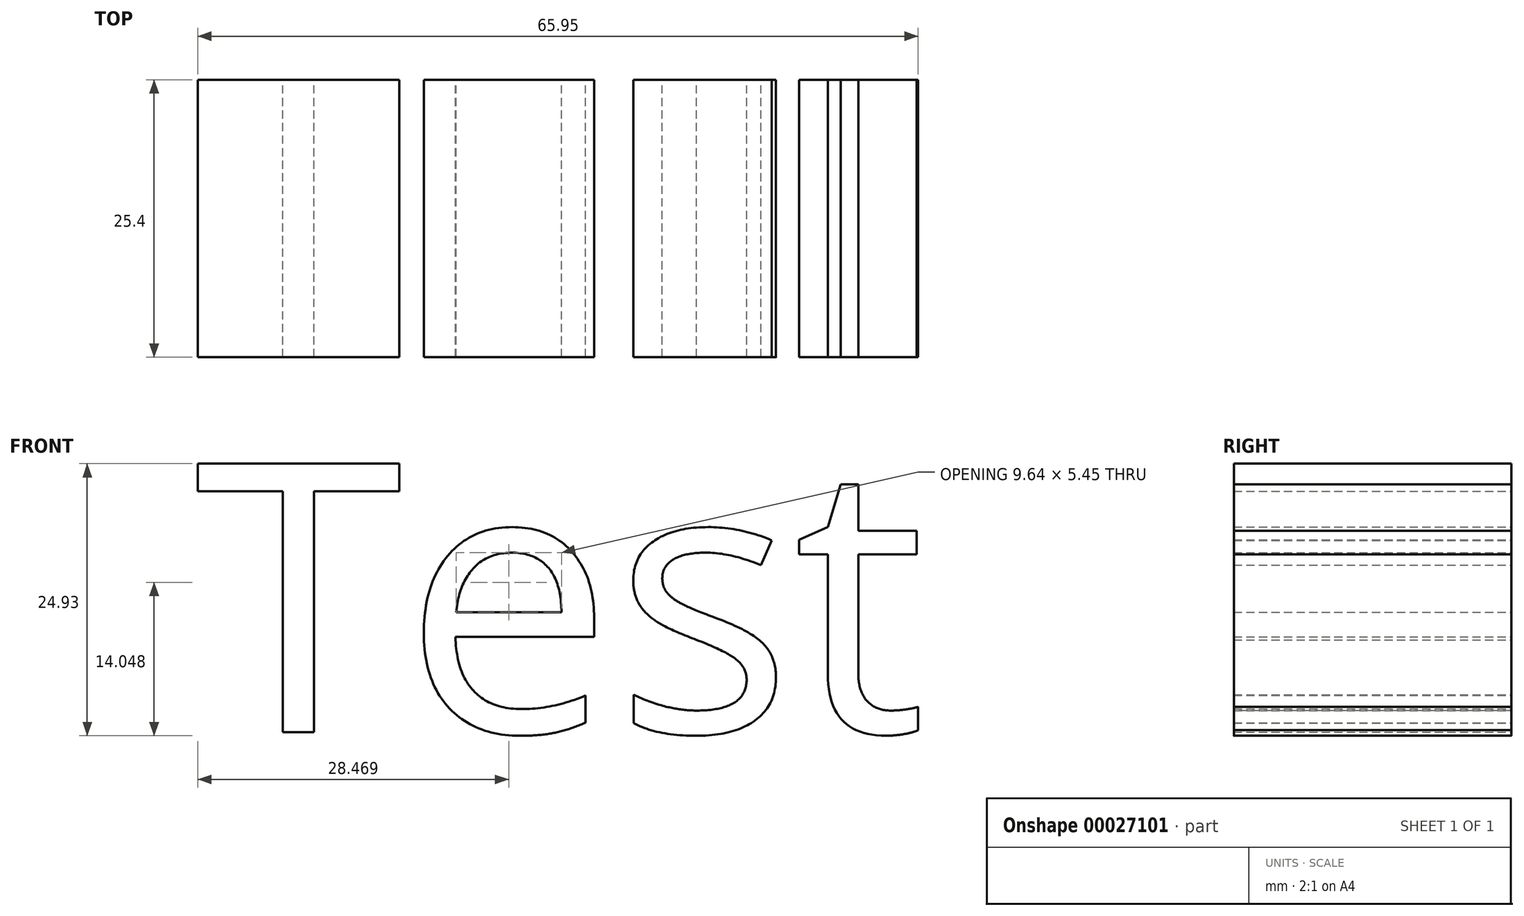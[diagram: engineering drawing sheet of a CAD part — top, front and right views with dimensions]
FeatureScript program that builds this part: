
annotation { "Feature Type Name" : "Feature", "Feature Type Description" : "" }
export const myFeature = defineFeature(function(context is Context, id is Id, definition is map)
    precondition{}
    {
        {
            var Q0;
            Q0=qCreatedBy(makeId("Front.planeOp"),FACE);
            var sketch = newSketch(context, id + "F0", { "sketchPlane" : qUnion([Q0])});
            skText(sketch, "E0", { "text": "Test", "fontName": "OpenSans-Regular.ttf"});
            const initialGuessF0  = {"E0": [-0.11136, -0.0248, 1, 0, 0.0248]};
            skSetInitialGuess(sketch, initialGuessF0);
            skSolve(sketch);
        }
        {
            var Q0;
            Q0 = qSketchRegion(id + "F0", true);
            extrude(context, id + "F1", {"entities" : qUnion([Q0]), "depth" : 25.4 * mm});
        }
    });
